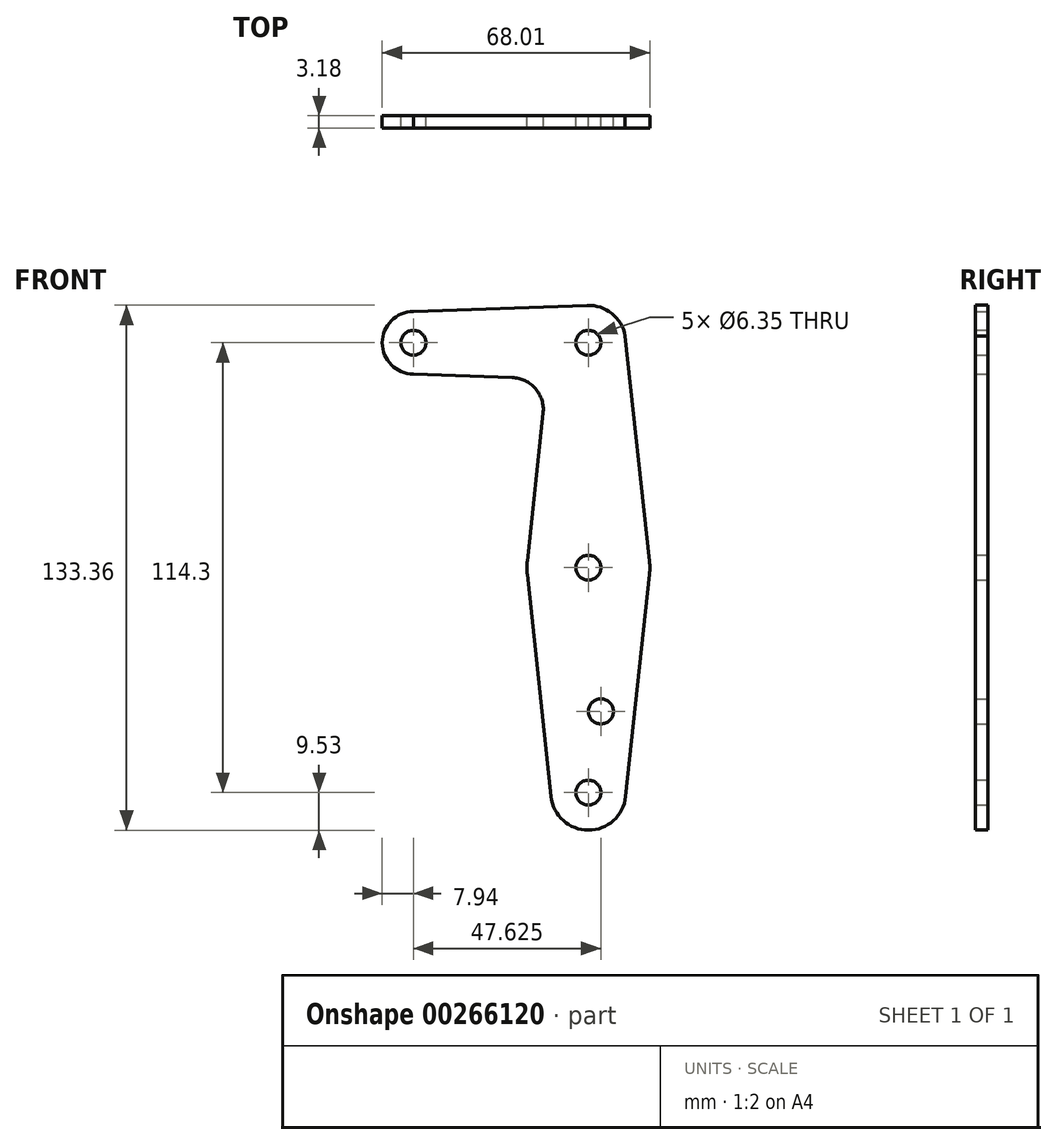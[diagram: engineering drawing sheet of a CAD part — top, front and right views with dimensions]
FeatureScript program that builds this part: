
annotation { "Feature Type Name" : "Feature", "Feature Type Description" : "" }
export const myFeature = defineFeature(function(context is Context, id is Id, definition is map)
    precondition{}
    {
        {
            var Q0;
            Q0=qCreatedBy(makeId("Front.planeOp"),FACE);
            var sketch = newSketch(context, id + "F0", { "sketchPlane" : qUnion([Q0])});
            skLineSegment(sketch, "E0", {"start": v(0, 0) * mm, "end": v(44.45, 0) * mm, "construction": true});
            skLineSegment(sketch, "E1", {"start": v(44.45, 0) * mm, "end": v(44.45, -114.3) * mm, "construction": true});
            skCircle(sketch, "E2", {"center": v(0, 0) * mm, "radius": 7.94 * mm});
            skCircle(sketch, "E3", {"center": v(0, 0) * mm, "radius": 3.18 * mm});
            skCircle(sketch, "E4", {"center": v(44.45, 0) * mm, "radius": 9.53 * mm});
            skCircle(sketch, "E5", {"center": v(44.45, 0) * mm, "radius": 3.18 * mm});
            skCircle(sketch, "E6", {"center": v(44.45, -57.15) * mm, "radius": 15.62 * mm});
            skCircle(sketch, "E7", {"center": v(44.45, -114.3) * mm, "radius": 9.53 * mm});
            skCircle(sketch, "E8", {"center": v(44.45, -114.3) * mm, "radius": 3.18 * mm});
            skCircle(sketch, "E9", {"center": v(44.45, -57.15) * mm, "radius": 3.18 * mm});
            skCircle(sketch, "E10", {"center": v(47.63, -93.66) * mm, "radius": 3.18 * mm});
            skLineSegment(sketch, "E11", {"start": v(0, 7.94) * mm, "end": v(44.1, 9.52) * mm});
            skLineSegment(sketch, "E12", {"start": v(34.98, -115.32) * mm, "end": v(28.92, -58.82) * mm});
            skLineSegment(sketch, "E13", {"start": v(59.98, -58.82) * mm, "end": v(53.92, -115.32) * mm});
            skLineSegment(sketch, "E14", {"start": v(53.8, 1.77) * mm, "end": v(59.98, -55.48) * mm});
            skLineSegment(sketch, "E15", {"start": v(0, -7.94) * mm, "end": v(25.1, -8.84) * mm});
            skLineSegment(sketch, "E16", {"start": v(28.92, -55.48) * mm, "end": v(32.95, -17.9) * mm});
            skArc(sketch, "E17.filletArc", {"start": v(32.95, -17.9) * mm, "mid": v(31, -11.66) * mm, "end": v(25.1, -8.84) * mm});
            skSolve(sketch);
        }
        {
            var Q0;
            {var subQ0=sQuery(id+"F0.wireOp",EDGE,"E11");var subQ1=sQuery(id+"F0.wireOp",EDGE,"E2");var subQ2=makeQuery(id+"F0.imprint","INTERSECT",VERTEX,{"disambiguationData":[OD(0.0)],"derivedFrom":[subQ1,subQ0]});Q0=makeQuery(id+"F0.imprint","IMPRINT",FACE,{"disambiguationData":[TD([[makeQuery(id+"F0.imprint","IMPRINT",EDGE,{"disambiguationData":[TD([[subQ2,1.0]])],"derivedFrom":subQ1}),1.0]])]});}
            var Q1;
            {var subQ0=sQuery(id+"F0.wireOp",EDGE,"E13");var subQ1=sQuery(id+"F0.wireOp",EDGE,"E6");var subQ3=makeQuery(id+"F0.imprint","INTERSECT",VERTEX,{"derivedFrom":[subQ1,subQ0]});Q1=makeQuery(id+"F0.imprint","IMPRINT",FACE,{"disambiguationData":[TD([[makeQuery(id+"F0.imprint","IMPRINT",EDGE,{"disambiguationData":[TD([[subQ3,-1.0]])],"derivedFrom":subQ1}),1.0]])]});}
            var Q2;
            {var subQ0=sQuery(id+"F0.wireOp",EDGE,"E14");var subQ1=sQuery(id+"F0.wireOp",EDGE,"E6");var subQ3=makeQuery(id+"F0.imprint","INTERSECT",VERTEX,{"derivedFrom":[subQ1,subQ0]});Q2=makeQuery(id+"F0.imprint","IMPRINT",FACE,{"disambiguationData":[TD([[makeQuery(id+"F0.imprint","IMPRINT",EDGE,{"disambiguationData":[TD([[subQ3,1.0]])],"derivedFrom":subQ1}),1.0]])]});}
            var Q3;
            Q3=makeQuery(id+"F0.imprint","IMPRINT",FACE,{"disambiguationData":[TD([[makeQuery(id+"F0.imprint","IMPRINT",EDGE,{"derivedFrom":sQuery(id+"F0.wireOp",EDGE,"E5")}),-1.0]])]});
            var Q4;
            Q4=makeQuery(id+"F0.imprint","IMPRINT",FACE,{"disambiguationData":[TD([[makeQuery(id+"F0.imprint","IMPRINT",EDGE,{"derivedFrom":sQuery(id+"F0.wireOp",EDGE,"E8")}),-1.0]])]});
            var Q5;
            Q5=makeQuery(id+"F0.imprint","IMPRINT",FACE,{"disambiguationData":[TD([[makeQuery(id+"F0.imprint","IMPRINT",EDGE,{"derivedFrom":sQuery(id+"F0.wireOp",EDGE,"E3")}),-1.0]])]});
            var Q6;
            Q6=makeQuery(id+"F0.imprint","IMPRINT",FACE,{"disambiguationData":[TD([[makeQuery(id+"F0.imprint","IMPRINT",EDGE,{"derivedFrom":sQuery(id+"F0.wireOp",EDGE,"E10")}),-1.0]])]});
            var Q7;
            Q7=makeQuery(id+"F0.imprint","IMPRINT",FACE,{"disambiguationData":[TD([[makeQuery(id+"F0.imprint","IMPRINT",EDGE,{"derivedFrom":sQuery(id+"F0.wireOp",EDGE,"E9")}),-1.0]])]});
            var Q8;
            {var subQ11=sQuery(id+"F0.wireOp",EDGE,"E15");Q8=makeQuery(id+"F0.imprint","IMPRINT",FACE,{"disambiguationData":[TD([[makeQuery(id+"F0.imprint","IMPRINT",EDGE,{"derivedFrom":subQ11}),1.0]])]});}
            extrude(context, id + "F1", {"entities" : qUnion([Q0, Q1, Q2, Q3, Q4, Q5, Q6, Q7, Q8]), "depth" : 3.17 * mm});
        }
    });
